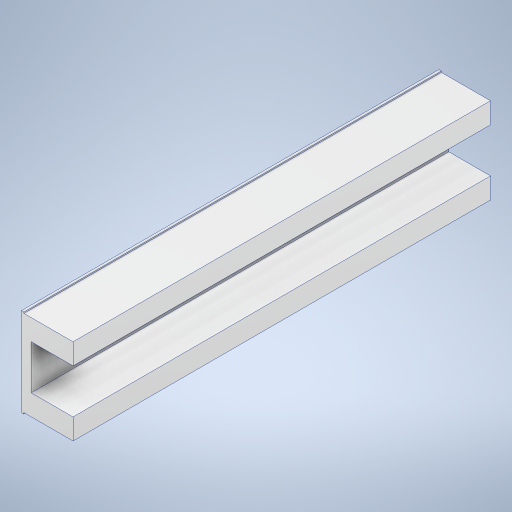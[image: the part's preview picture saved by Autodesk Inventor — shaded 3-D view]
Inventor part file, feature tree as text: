
AUTODESK INVENTOR PART (.ipt)
format: ipt  version: 2024 (Build 280153000, 153)  size: 351,744 bytes
history: native  units: mm
features: extrude x7, sketch x7, projected_geometry x3
ambient origin geometry x8: Origin, YZ Plane, XZ Plane, XY Plane, X Axis, Y Axis, Z Axis, Center Point
bodies: Solid1 (feature_tree)
feature tree (17):
  extrude  "Extrusion1"  Depth=160.0mm TaperAngle=0.0deg
  extrude  "Extrusion2"  Depth=25.0mm
  extrude  "Extrusion3"  Depth=45.0mm
  extrude  "Extrusion4"  Depth=4.0mm
  extrude  "Extrusion5"  Depth=36.0mm
  extrude  "Extrusion6"  Depth=150.0mm TaperAngle=0.0deg
  extrude  "Extrusion7"  Depth=340.0mm
  sketch  "Sketch1"  dims[d0=475.0mm d1=160.0mm d2=0.0mm]
  sketch  "Sketch2"  dims[d4=25.0mm d5=25.0mm]
  sketch  "Sketch3"  dims[d6=10.0mm d7=45.0mm]
  sketch  "Sketch4"  dims[d8=45.0mm d9=4.0mm]
  projected_geometry  "Projected Loop1"
  projected_geometry  "Projected Loop2"
  sketch  "Sketch5"  dims[d10=36.0mm d11=80.0mm]
  projected_geometry  "Projected Loop3"
  sketch  "Sketch6"  dims[d12=80.0mm d13=150.0mm d14=0.0mm]
  sketch  "Sketch7"  dims[d15=20.0mm d16=340.0mm d17=200.0mm d18=0.0mm d19=30.0mm d20=0.0mm d21=5.0mm d22=0.0mm d23=13.0mm d24=13.0mm d25=3.0mm d26=500.0mm d27=0.0mm d28=1.0mm d29=1.0mm d30=2.0mm d31=1000.0mm d32=0.0mm]
